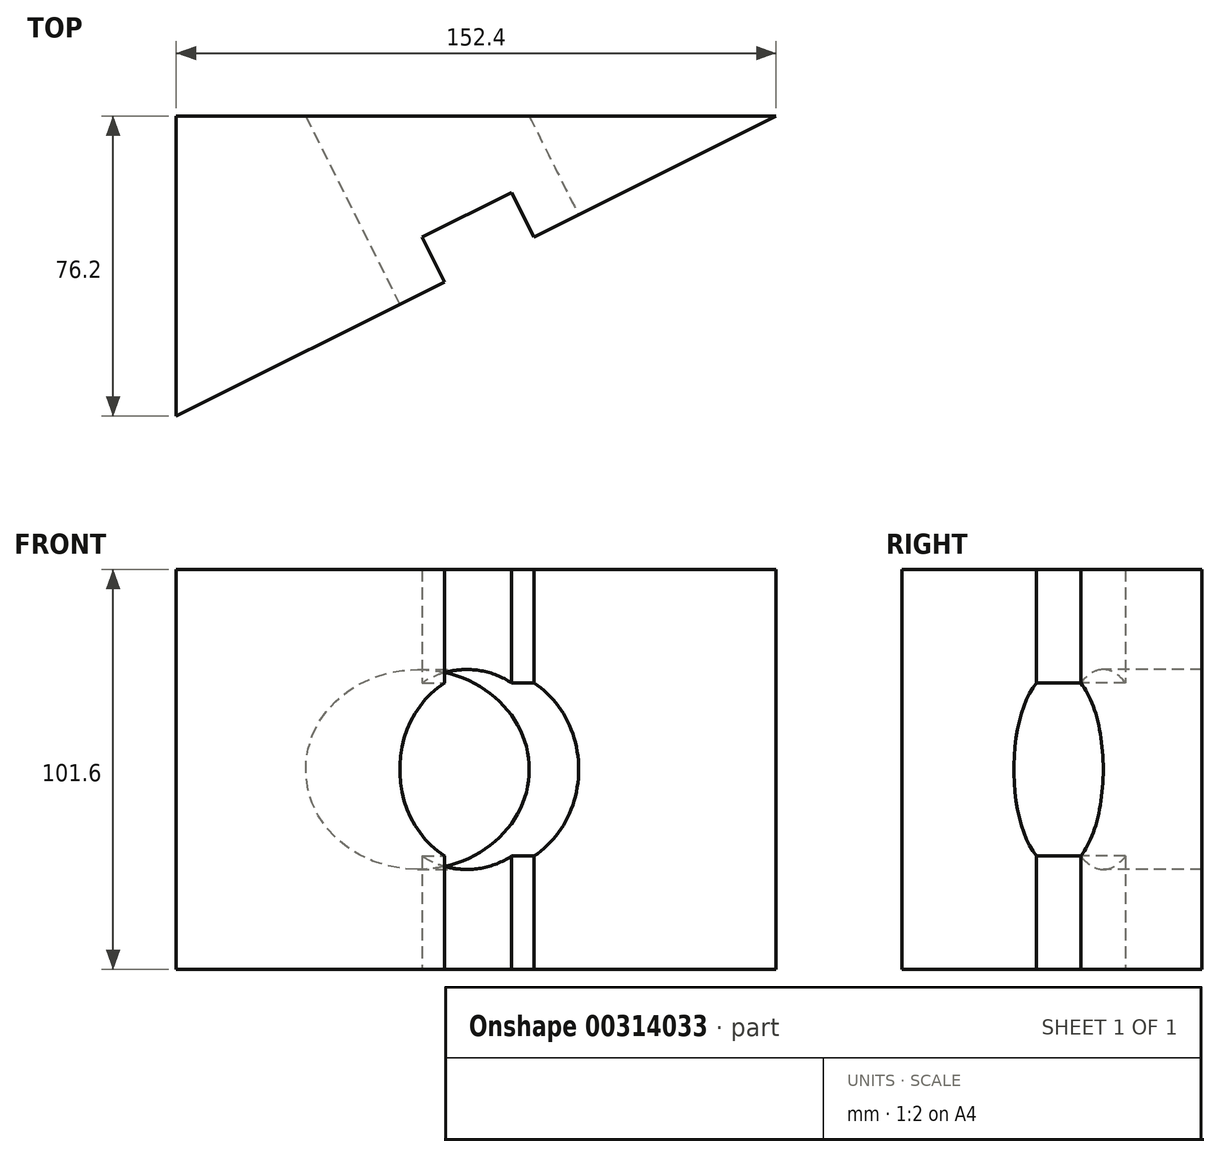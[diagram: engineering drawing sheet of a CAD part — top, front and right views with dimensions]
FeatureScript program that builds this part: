
annotation { "Feature Type Name" : "Feature", "Feature Type Description" : "" }
export const myFeature = defineFeature(function(context is Context, id is Id, definition is map)
    precondition{}
    {
        {
            var Q0;
            Q0=qCreatedBy(makeId("Top.planeOp"),FACE);
            var sketch = newSketch(context, id + "F0", { "sketchPlane" : qUnion([Q0])});
            skLineSegment(sketch, "E0.bottom", {"start": v(0, 0) * mm, "end": v(152.4, 0) * mm});
            skLineSegment(sketch, "E0.top", {"start": v(0, -76.2) * mm, "end": v(152.4, -76.2) * mm});
            skLineSegment(sketch, "E0.left", {"start": v(0, 0) * mm, "end": v(0, -76.2) * mm});
            skLineSegment(sketch, "E0.right", {"start": v(152.4, 0) * mm, "end": v(152.4, -76.2) * mm});
            skLineSegment(sketch, "E1", {"start": v(0, -76.2) * mm, "end": v(152.4, 0) * mm});
            skSolve(sketch);
        }
        {
            var Q0;
            Q0=makeQuery(id+"F0.imprint","IMPRINT",FACE,{"disambiguationData":[TD([[makeQuery(id+"F0.imprint","IMPRINT",EDGE,{"derivedFrom":sQuery(id+"F0.wireOp",EDGE,"E0.bottom")}),-1.0]])]});
            extrude(context, id + "F1", {"entities" : qUnion([Q0]), "depth" : 101.6 * mm});
        }
        {
            var Q0;
            Q0=makeQuery(id+"F1.opExtrude","SWEPT_FACE",FACE,{"disambiguationData":[OSD([sQuery(id+"F0.wireOp",EDGE,"E1")])]});
            var sketch = newSketch(context, id + "F2", { "sketchPlane" : qUnion([Q0])});
            skLineSegment(sketch, "E2.bottom", {"start": v(42.12, 101.6) * mm, "end": v(67.52, 101.6) * mm});
            skLineSegment(sketch, "E2.top", {"start": v(42.12, 0) * mm, "end": v(67.52, 0) * mm});
            skLineSegment(sketch, "E2.left", {"start": v(42.12, 101.6) * mm, "end": v(42.12, 0) * mm});
            skLineSegment(sketch, "E2.right", {"start": v(67.52, 101.6) * mm, "end": v(67.52, 0) * mm});
            skPoint(sketch, "E2.middle", {"position": v(54.82, 50.8) * mm});
            skPoint(sketch, "E2.middle.positionSnap0", {"position": v(-34.08, 50.8) * mm});
            skPoint(sketch, "E2.centerSnap0", {"position": v(-34.08, 50.8) * mm});
            skSolve(sketch);
        }
        {
            var Q0;
            Q0=makeQuery(id+"F2.imprint","IMPRINT",FACE,{"disambiguationData":[TD([[makeQuery(id+"F2.imprint","IMPRINT",EDGE,{"derivedFrom":sQuery(id+"F2.wireOp",EDGE,"E2.bottom")}),-1.0]])]});
            extrude(context, id + "F3", {"entities" : qUnion([Q0]), "operationType" : NewBodyOperationType.REMOVE, "oppositeDirection" : true, "depth" : 12.7 * mm});
        }
        {
            var Q0;
            {var subQ0=sQuery(id+"F0.wireOp",EDGE,"E1");var subQ1=sQuery(id+"F0.wireOp",EDGE,"E0.left");Q0=makeQuery(id+"F3.boolean.opBoolean","SPLIT",FACE,{"disambiguationData":[TD([makeQuery(id+"F1.opExtrude","SWEPT_FACE",FACE,{"disambiguationData":[OSD([subQ1])]})])],"derivedFrom":makeQuery(id+"F1.opExtrude","SWEPT_FACE",FACE,{"disambiguationData":[OSD([subQ0])]})});}
            var sketch = newSketch(context, id + "F4", { "sketchPlane" : qUnion([Q0])});
            skCircle(sketch, "E3", {"center": v(54.82, 50.8) * mm, "radius": 25.4 * mm});
            skSolve(sketch);
        }
        {
            var Q0;
            {var subQ0=sQuery(id+"F4.wireOp",EDGE,"E3");var subQ1=makeQuery(id+"F3.boolean.opBoolean","COPY",EDGE,{"derivedFrom":makeQuery(id+"F3.opExtrude","CAP_EDGE",EDGE,{"disambiguationData":[OSD([sQuery(id+"F2.wireOp",EDGE,"E2.left")])],"isStart":true})});var subQ2=makeQuery(id+"F4.imprint","INTERSECT",VERTEX,{"disambiguationData":[OD(0.0)],"derivedFrom":[subQ1,subQ0]});Q0=makeQuery(id+"F4.imprint","IMPRINT",FACE,{"disambiguationData":[TD([[makeQuery(id+"F4.imprint","IMPRINT",EDGE,{"disambiguationData":[TD([[subQ2,-1.0]])],"derivedFrom":subQ0}),1.0]])]});}
            var Q1;
            {var subQ0=sQuery(id+"F4.wireOp",EDGE,"E3");var subQ1=makeQuery(id+"F3.boolean.opBoolean","COPY",EDGE,{"derivedFrom":makeQuery(id+"F3.opExtrude","CAP_EDGE",EDGE,{"disambiguationData":[OSD([sQuery(id+"F2.wireOp",EDGE,"E2.left")])],"isStart":true})});var subQ2=makeQuery(id+"F4.imprint","INTERSECT",VERTEX,{"disambiguationData":[OD(0.0)],"derivedFrom":[subQ1,subQ0]});Q1=makeQuery(id+"F4.imprint","IMPRINT",FACE,{"disambiguationData":[TD([[makeQuery(id+"F4.imprint","IMPRINT",EDGE,{"disambiguationData":[TD([[subQ2,1.0]])],"derivedFrom":subQ0}),1.0]])]});}
            extrude(context, id + "F5", {"entities" : qUnion([Q0, Q1]), "operationType" : NewBodyOperationType.REMOVE, "endBound" : BoundingType.THROUGH_ALL, "oppositeDirection" : true, "depth" : 25.4 * mm});
        }
    });
